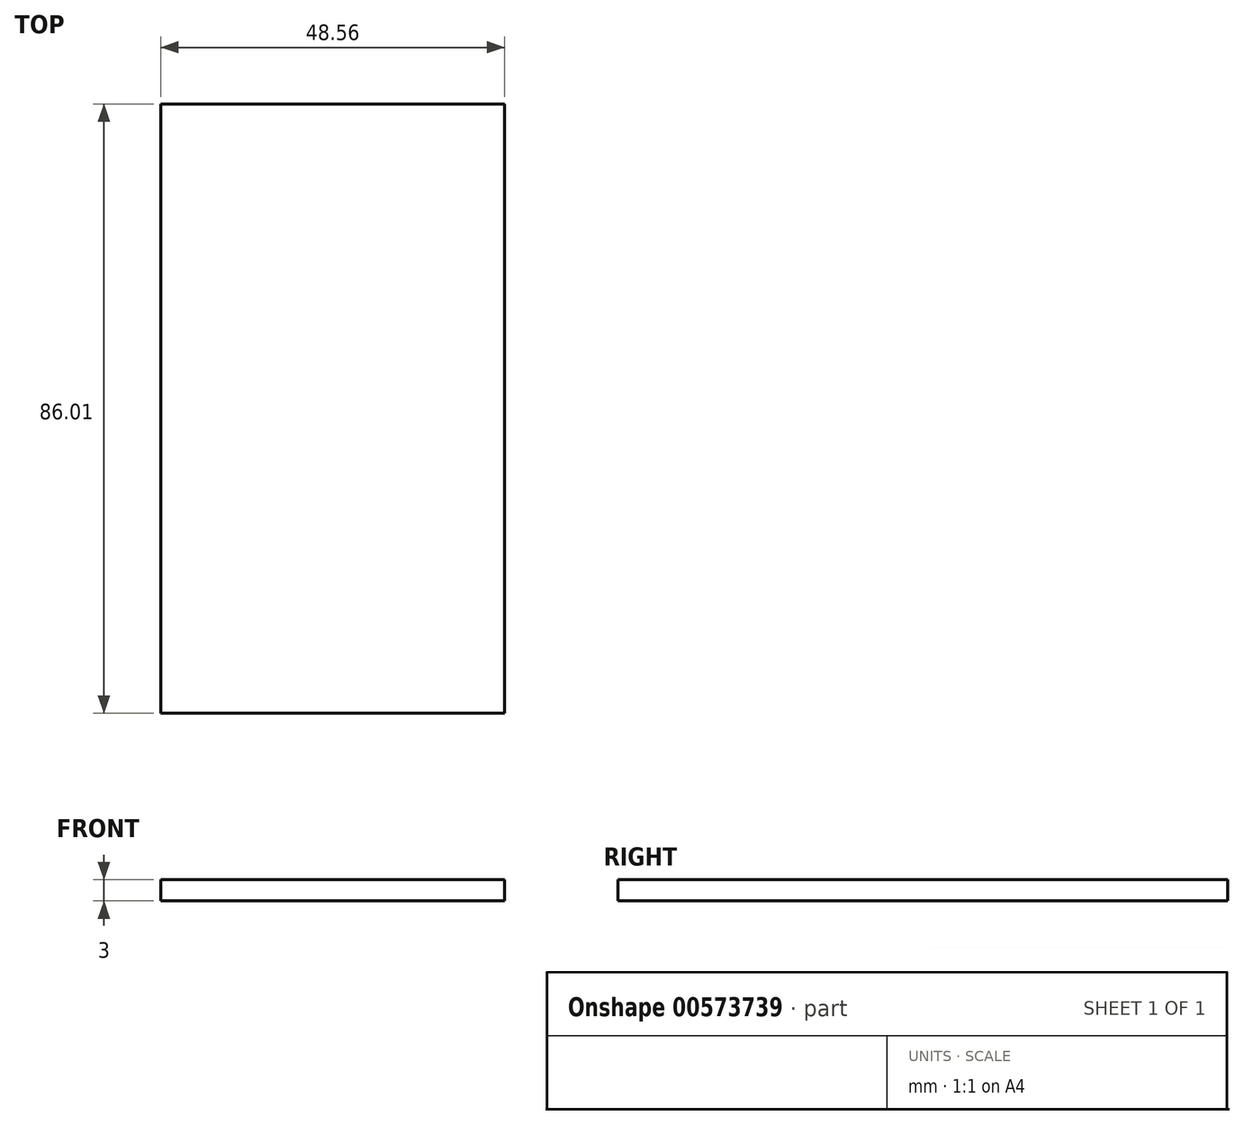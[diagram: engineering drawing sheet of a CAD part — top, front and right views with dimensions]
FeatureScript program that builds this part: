
annotation { "Feature Type Name" : "Feature", "Feature Type Description" : "" }
export const myFeature = defineFeature(function(context is Context, id is Id, definition is map)
    precondition{}
    {
        {
            var Q0;
            Q0=qCreatedBy(makeId("Top.planeOp"),FACE);
            var sketch = newSketch(context, id + "F0", { "sketchPlane" : qUnion([Q0])});
            skLineSegment(sketch, "E0.bottom", {"start": v(0, 0) * mm, "end": v(48.56, 0) * mm});
            skLineSegment(sketch, "E0.top", {"start": v(0, 86) * mm, "end": v(48.56, 86) * mm});
            skLineSegment(sketch, "E0.left", {"start": v(0, 0) * mm, "end": v(0, 86) * mm});
            skLineSegment(sketch, "E0.right", {"start": v(48.56, 0) * mm, "end": v(48.56, 86) * mm});
            skSolve(sketch);
        }
        {
            var Q0;
            Q0=makeQuery(id+"F0.imprint","IMPRINT",FACE,{"disambiguationData":[TD([[makeQuery(id+"F0.imprint","IMPRINT",EDGE,{"derivedFrom":sQuery(id+"F0.wireOp",EDGE,"E0.bottom")}),1.0]])]});
            extrude(context, id + "F1", {"entities" : qUnion([Q0]), "depth" : 3 * mm, "offsetDistance" : 25.4 * mm});
        }
    });
